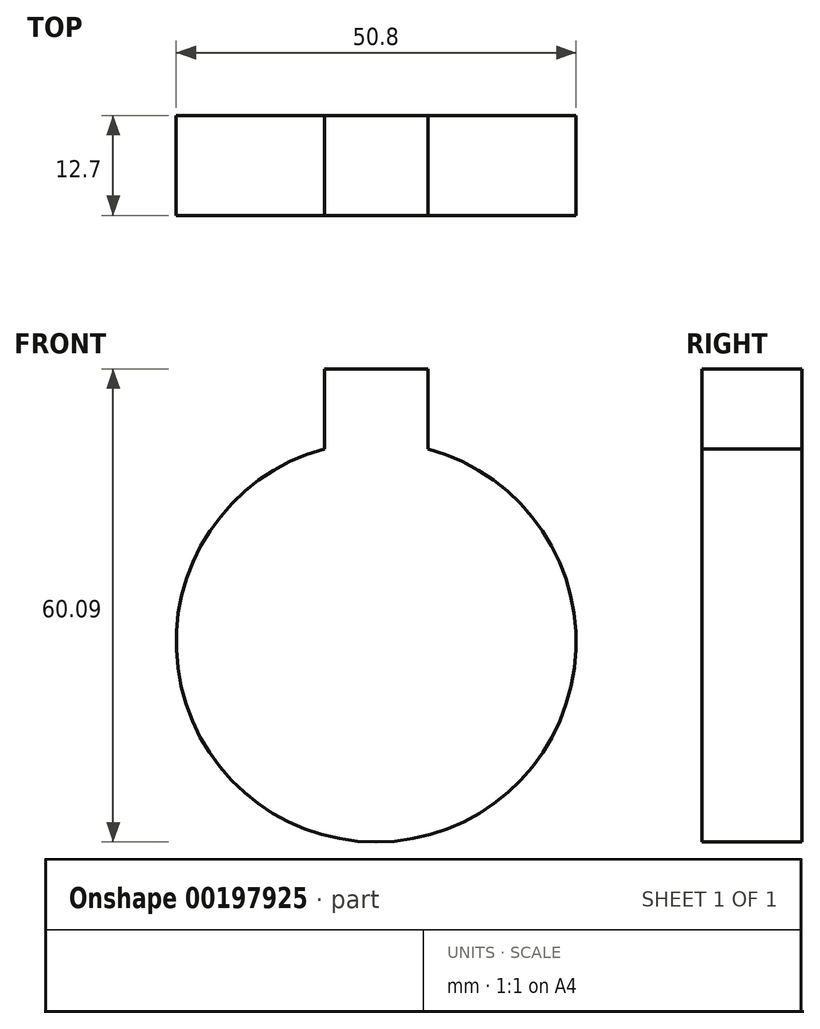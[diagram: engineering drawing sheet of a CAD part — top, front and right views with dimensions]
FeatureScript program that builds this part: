
annotation { "Feature Type Name" : "Feature", "Feature Type Description" : "" }
export const myFeature = defineFeature(function(context is Context, id is Id, definition is map)
    precondition{}
    {
        {
            var Q0;
            Q0=qCreatedBy(makeId("Front.planeOp"),FACE);
            var sketch = newSketch(context, id + "F0", { "sketchPlane" : qUnion([Q0])});
            skCircle(sketch, "E0", {"center": v(0, 0) * mm, "radius": 25.4 * mm});
            skSolve(sketch);
        }
        {
            var Q0;
            Q0 = qSketchRegion(id + "F0", true);
            extrude(context, id + "F1", {"entities" : qUnion([Q0]), "endBound" : BoundingType.SYMMETRIC, "depth" : 12.7 * mm});
        }
        {
            var Q0;
            Q0=makeQuery(id+"F1.opExtrude","CAP_FACE",FACE,{"disambiguationData":[OSD([sQuery(id+"F0.wireOp",EDGE,"E0")])],"isStart":false});
            var sketch = newSketch(context, id + "F2", { "sketchPlane" : qUnion([Q0])});
            skLineSegment(sketch, "E1", {"start": v(0, 25.4) * mm, "end": v(0, 0) * mm});
            skLineSegment(sketch, "E2", {"start": v(0, 0) * mm, "end": v(6.57, 24.53) * mm});
            skLineSegment(sketch, "E3", {"start": v(0, 0) * mm, "end": v(-6.57, 24.53) * mm});
            skLineSegment(sketch, "E4", {"start": v(-6.57, 24.53) * mm, "end": v(6.57, 24.53) * mm});
            skLineSegment(sketch, "E5.0", {"start": v(-6.57, 34.7) * mm, "end": v(6.57, 34.7) * mm});
            skLineSegment(sketch, "E6", {"start": v(-6.57, 24.53) * mm, "end": v(-6.57, 34.7) * mm});
            skLineSegment(sketch, "E7", {"start": v(6.57, 34.7) * mm, "end": v(6.57, 24.53) * mm});
            skSolve(sketch);
        }
        {
            var Q0;
            Q0=makeQuery(id+"F2.imprint","IMPRINT",FACE,{"disambiguationData":[TD([[makeQuery(id+"F2.imprint","IMPRINT",EDGE,{"derivedFrom":sQuery(id+"F2.wireOp",EDGE,"E5.0")}),-1.0]])]});
            extrude(context, id + "F3", {"entities" : qUnion([Q0]), "operationType" : NewBodyOperationType.ADD, "oppositeDirection" : true, "depth" : 12.7 * mm});
        }
    });
